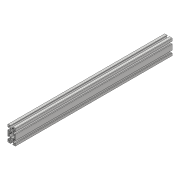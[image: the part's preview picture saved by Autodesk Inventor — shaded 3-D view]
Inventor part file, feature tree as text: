
AUTODESK INVENTOR PART (.ipt)
format: ipt  version: 2018 (Build 220112000, 112)  size: 242,176 bytes
history: native  units: mm
features: extrude x1, sketch x1
ambient origin geometry x8: Origin, YZ Plane, XZ Plane, XY Plane, X Axis, Y Axis, Z Axis, Center Point
bodies: Solid1 (feature_tree)
feature tree (2):
  extrude  "Extrusion1"  [1 undecoded]
  sketch  "Sketch1"  dims[d0=400.0mm d1=0.0mm]
note: 1 required parameter value undecoded (feature->parameter linkage not recoverable at this tier; creation-order binding heuristic only, values carry confidence <= 0.55)
